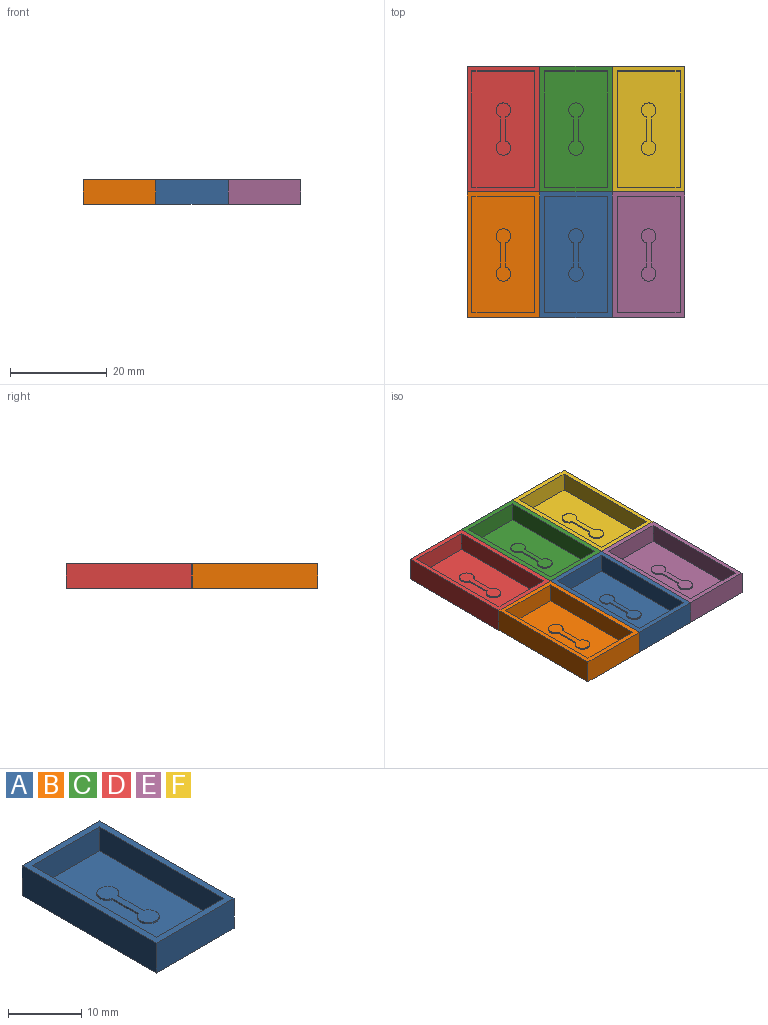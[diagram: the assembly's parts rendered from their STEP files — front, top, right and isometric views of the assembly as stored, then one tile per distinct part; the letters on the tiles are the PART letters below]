
ASSEMBLY  parts=6 mates=4
PART A: 16 faces, bbox 15x26x5 mm
  f0: plane 5x0.25mm, normal (1,0,0), area 1.2mm2, adj f1,f3,f4,f5
  f1: cylinder r=1.5mm len=3mm, axis (0,0,-1), area 2.1mm2, adj f0,f2,f4,f5
  f2: plane 5x0.25mm, normal (-1,0,0), area 1.2mm2, adj f1,f3,f4,f5
  f3: cylinder r=1.5mm len=3mm, axis (0,0,-1), area 2.1mm2, adj f0,f2,f4,f5
  f4: plane 10.83x3mm, normal (0,0,1), area 19mm2, adj f0,f1,f2,f3
  f5: plane 24x13mm, normal (0,0,1), area 293mm2, adj f0,f1,f2,f3,f6,f7,f8,f9
  f6: plane 13x4mm, normal (0,1,0), area 52mm2, adj f5,f7,f9,f10
  f7: plane 24x4mm, normal (1,0,0), area 96mm2, adj f5,f6,f8,f10
  f8: plane 13x4mm, normal (0,-1,0), area 52mm2, adj f5,f7,f9,f10
  f9: plane 24x4mm, normal (-1,0,0), area 96mm2, adj f5,f6,f8,f10
  f10: plane 26x15mm, normal (0,0,1), area 78mm2, adj f6,f7,f8,f9,f12,f13,f14,f15
  f11: plane 26x15mm, normal (0,0,-1), area 390mm2, adj f12,f13,f14,f15
  f12: plane 26x5mm, normal (1,0,0), area 130mm2, adj f10,f11,f13,f15
  f13: plane 15x5mm, normal (0,-1,0), area 75mm2, adj f10,f11,f12,f14
  f14: plane 26x5mm, normal (-1,0,0), area 130mm2, adj f10,f11,f13,f15
  f15: plane 15x5mm, normal (0,1,0), area 75mm2, adj f10,f11,f12,f14
PART B: same geometry as A
PART C: same geometry as A
PART D: same geometry as A
PART E: same geometry as A
PART F: same geometry as A
PLACE A t=(7.5,-13,1)mm
PLACE B t=(-7.5,-13,1)mm
PLACE C t=(7.5,13,1)mm
PLACE D t=(-7.5,13,1)mm
PLACE E t=(22.5,-13,1)mm
PLACE F t=(22.5,13,1)mm
MATE fastened F.f12 <-> E.f12  axis (1,0,0) through (30,0,2.5)mm
MATE planar B.f10 <-> A.f10  axis (0,0,1) through (0,0,5)mm
MATE planar B.f10 <-> C.f10  axis (0,0,1) through (0,0,5)mm
MATE fastened A.f13 <-> E.f13  axis (0,-1,0) through (15,-26,2.5)mm
